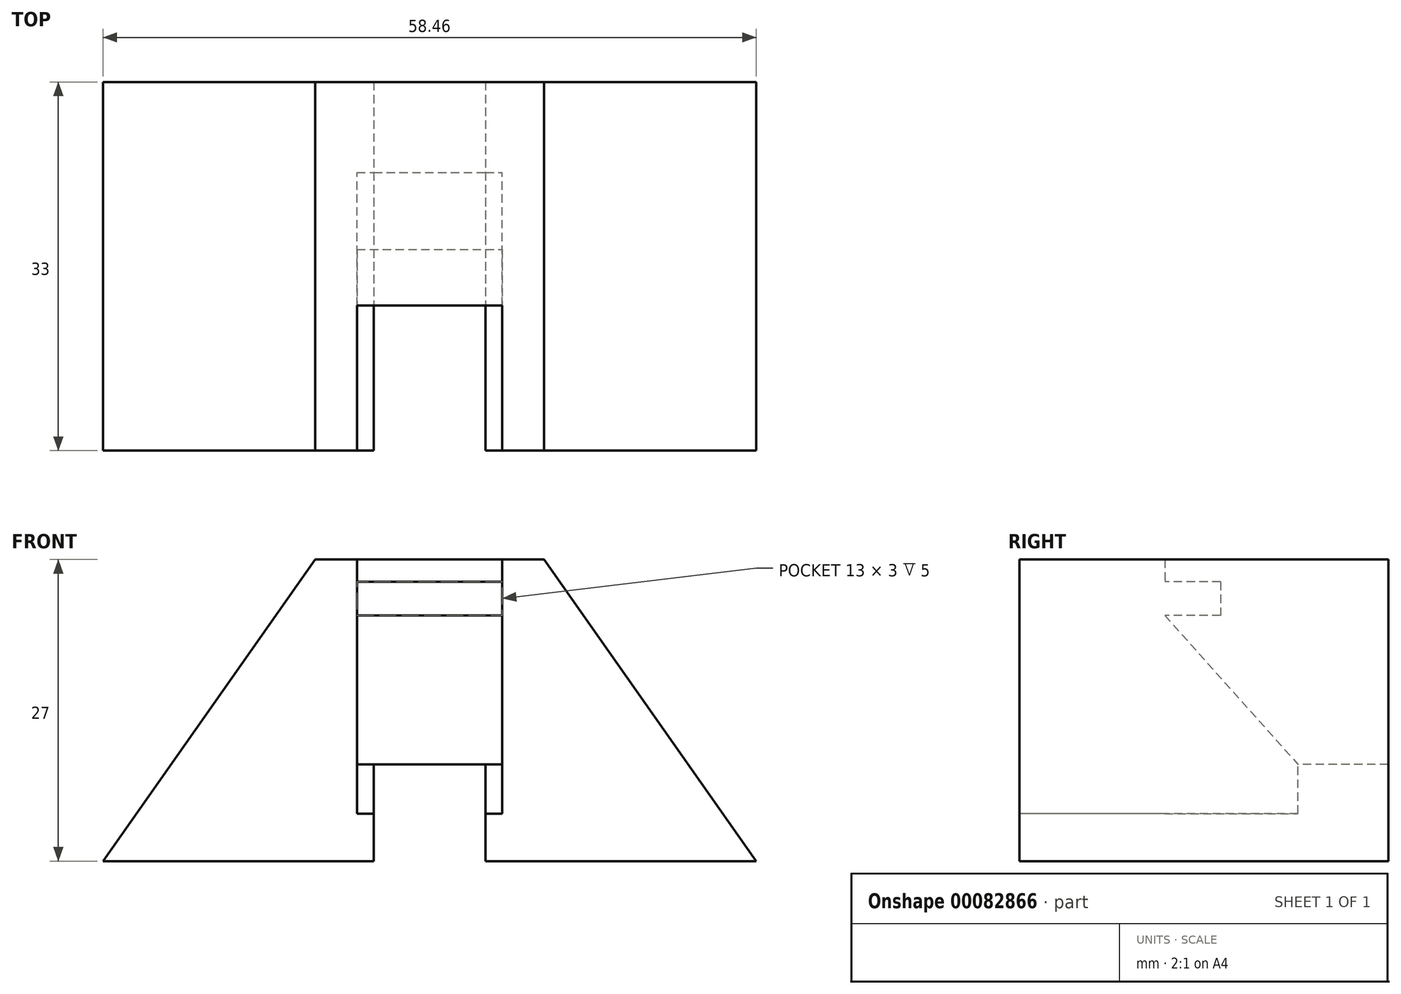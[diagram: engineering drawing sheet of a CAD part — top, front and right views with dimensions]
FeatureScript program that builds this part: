
annotation { "Feature Type Name" : "Feature", "Feature Type Description" : "" }
export const myFeature = defineFeature(function(context is Context, id is Id, definition is map)
    precondition{}
    {
        {
            var Q0;
            Q0=qCreatedBy(makeId("Top.planeOp"),FACE);
            var sketch = newSketch(context, id + "F0", { "sketchPlane" : qUnion([Q0])});
            skLineSegment(sketch, "E0.bottom", {"start": v(-29.22, 16.5) * mm, "end": v(29.23, 16.5) * mm});
            skLineSegment(sketch, "E0.top", {"start": v(-29.23, -16.5) * mm, "end": v(29.23, -16.5) * mm});
            skLineSegment(sketch, "E0.left", {"start": v(-29.23, 16.5) * mm, "end": v(-29.23, -16.5) * mm});
            skLineSegment(sketch, "E0.right", {"start": v(29.23, 16.5) * mm, "end": v(29.23, -16.5) * mm});
            skSolve(sketch);
        }
        {
            var Q0;
            Q0=qSketchRegion(id+"F0",true);
            extrude(context, id + "F1", {"entities" : qUnion([Q0]), "depth" : 27 * mm});
        }
        {
            var Q0;
            Q0=makeQuery(id+"F1.opExtrude","SWEPT_FACE",FACE,{"disambiguationData":[OSD([sQuery(id+"F0.wireOp",EDGE,"E0.top")])]});
            var sketch = newSketch(context, id + "F2", { "sketchPlane" : qUnion([Q0])});
            skLineSegment(sketch, "E1", {"start": v(-29.23, 0) * mm, "end": v(-10.25, 27) * mm});
            skLineSegment(sketch, "E2", {"start": v(29.22, 0) * mm, "end": v(10.25, 27) * mm});
            skSolve(sketch);
        }
        {
            var Q0;
            Q0=qSketchRegion(id+"F2",true);
            var Q1;
            {var subQ0=sQuery(id+"F2.wireOp",EDGE,"E1");Q1=makeQuery(id+"F2.imprint","IMPRINT",FACE,{"disambiguationData":[TD([[makeQuery(id+"F2.imprint","IMPRINT",EDGE,{"derivedFrom":subQ0}),1.0]])]});}
            var Q2;
            {var subQ0=sQuery(id+"F2.wireOp",EDGE,"E2");Q2=makeQuery(id+"F2.imprint","IMPRINT",FACE,{"disambiguationData":[TD([[makeQuery(id+"F2.imprint","IMPRINT",EDGE,{"derivedFrom":subQ0}),-1.0]])]});}
            extrude(context, id + "F3", {"entities" : qUnion([Q0, Q1, Q2]), "operationType" : NewBodyOperationType.REMOVE, "endBound" : BoundingType.THROUGH_ALL, "oppositeDirection" : true, "depth" : 25 * mm});
        }
        {
            var Q0;
            Q0=makeQuery(id+"F1.opExtrude","SWEPT_FACE",FACE,{"disambiguationData":[OSD([sQuery(id+"F0.wireOp",EDGE,"E0.top")])]});
            var sketch = newSketch(context, id + "F4", { "sketchPlane" : qUnion([Q0])});
            skLineSegment(sketch, "E3.bottom", {"start": v(-5, 8.67) * mm, "end": v(5, 8.67) * mm});
            skLineSegment(sketch, "E3.top", {"start": v(-5, 0) * mm, "end": v(5, 0) * mm});
            skLineSegment(sketch, "E3.left", {"start": v(-5, 8.67) * mm, "end": v(-5, 0) * mm});
            skLineSegment(sketch, "E3.right", {"start": v(5, 8.67) * mm, "end": v(5, 0) * mm});
            skSolve(sketch);
        }
        {
            var Q0;
            Q0=qSketchRegion(id+"F4",true);
            extrude(context, id + "F5", {"entities" : qUnion([Q0]), "operationType" : NewBodyOperationType.REMOVE, "endBound" : BoundingType.THROUGH_ALL, "oppositeDirection" : true, "depth" : 25 * mm});
        }
        {
            var Q0;
            Q0=makeQuery(id+"F1.opExtrude","SWEPT_FACE",FACE,{"disambiguationData":[OSD([sQuery(id+"F0.wireOp",EDGE,"E0.top")])]});
            var sketch = newSketch(context, id + "F6", { "sketchPlane" : qUnion([Q0])});
            skLineSegment(sketch, "E4.bottom", {"start": v(-6.5, 27) * mm, "end": v(6.5, 27) * mm});
            skLineSegment(sketch, "E4.top", {"start": v(-6.5, 4.25) * mm, "end": v(6.5, 4.25) * mm});
            skLineSegment(sketch, "E4.left", {"start": v(-6.5, 27) * mm, "end": v(-6.5, 4.25) * mm});
            skLineSegment(sketch, "E4.right", {"start": v(6.5, 27) * mm, "end": v(6.5, 4.25) * mm});
            skSolve(sketch);
        }
        {
            var Q0;
            Q0=qSketchRegion(id+"F6",true);
            extrude(context, id + "F7", {"entities" : qUnion([Q0]), "operationType" : NewBodyOperationType.REMOVE, "oppositeDirection" : true, "depth" : 13 * mm});
        }
        {
            var Q0;
            Q0=makeQuery(id+"F7.boolean.opBoolean","COPY",FACE,{"derivedFrom":makeQuery(id+"F7.opExtrude","CAP_FACE",FACE,{"disambiguationData":[OSD([sQuery(id+"F6.wireOp",EDGE,"E4.bottom"),sQuery(id+"F6.wireOp",EDGE,"E4.top"),sQuery(id+"F6.wireOp",EDGE,"E4.left"),sQuery(id+"F6.wireOp",EDGE,"E4.right")])],"isStart":false})});
            var sketch = newSketch(context, id + "F8", { "sketchPlane" : qUnion([Q0])});
            skLineSegment(sketch, "E5.bottom", {"start": v(-6.5, 25) * mm, "end": v(6.5, 25) * mm});
            skLineSegment(sketch, "E5.top", {"start": v(-6.5, 22) * mm, "end": v(6.5, 22) * mm});
            skLineSegment(sketch, "E5.left", {"start": v(-6.5, 25) * mm, "end": v(-6.5, 22) * mm});
            skLineSegment(sketch, "E5.right", {"start": v(6.5, 25) * mm, "end": v(6.5, 22) * mm});
            skSolve(sketch);
        }
        {
            var Q0;
            Q0=qSketchRegion(id+"F8",true);
            extrude(context, id + "F9", {"entities" : qUnion([Q0]), "operationType" : NewBodyOperationType.REMOVE, "oppositeDirection" : true, "depth" : 5 * mm});
        }
        {
            var Q0;
            Q0=qCreatedBy(makeId("Right.planeOp"),FACE);
            var sketch = newSketch(context, id + "F10", { "sketchPlane" : qUnion([Q0])});
            skLineSegment(sketch, "E6", {"start": v(-3.5, 22) * mm, "end": v(-3.5, 4.25) * mm});
            skLineSegment(sketch, "E7", {"start": v(-3.5, 22) * mm, "end": v(8.41, 8.67) * mm});
            skLineSegment(sketch, "E8", {"start": v(-3.5, 4.25) * mm, "end": v(8.41, 4.25) * mm});
            skLineSegment(sketch, "E9", {"start": v(8.41, 8.67) * mm, "end": v(8.41, 4.25) * mm});
            skSolve(sketch);
        }
        {
            var Q0;
            Q0=qSketchRegion(id+"F10",true);
            extrude(context, id + "F11", {"entities" : qUnion([Q0]), "operationType" : NewBodyOperationType.REMOVE, "endBound" : BoundingType.SYMMETRIC, "oppositeDirection" : true, "depth" : 13 * mm});
        }
    });
